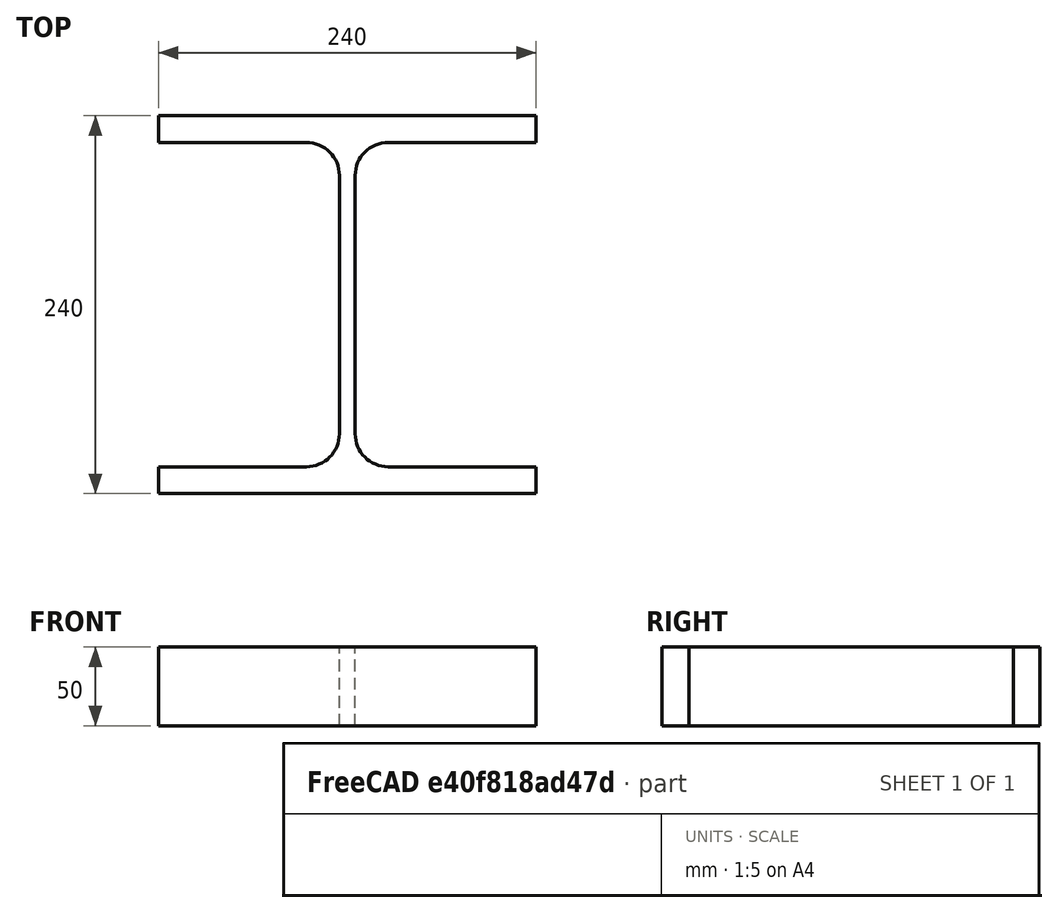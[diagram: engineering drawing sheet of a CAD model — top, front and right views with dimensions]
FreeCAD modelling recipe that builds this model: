
FCSTD DOCUMENT  (FreeCAD 0.15R4671 (Git))
Label: HE-B-Profile 240 DIN1025-2 S235JR
License: All rights reserved
LicenseURL: http://en.wikipedia.org/wiki/All_rights_reserved
objects: Sketcher::SketchObject×1, Part::Extrusion×1
note: 2 computed .brp shape members not serialized (recipe doc carries the construction recipe); baked Part::Feature solids carry a one-line shape summary decoded from their .brp

FEATURE [Sketcher::SketchObject] Sketch
  sketch-geometry (16):
    g0: LineSegment StartX=5 StartY=-82 StartZ=0 EndX=5 EndY=82 EndZ=0
    g1: LineSegment StartX=26 StartY=103 StartZ=0 EndX=120 EndY=103 EndZ=0
    g2: LineSegment StartX=120 StartY=103 StartZ=0 EndX=120 EndY=120 EndZ=0
    g3: LineSegment StartX=120 StartY=120 StartZ=0 EndX=-120 EndY=120 EndZ=0
    g4: LineSegment StartX=-120 StartY=120 StartZ=0 EndX=-120 EndY=103 EndZ=0
    g5: LineSegment StartX=-120 StartY=103 StartZ=0 EndX=-26 EndY=103 EndZ=0
    g6: LineSegment StartX=-5 StartY=82 StartZ=0 EndX=-5 EndY=-82 EndZ=0
    g7: LineSegment StartX=-26 StartY=-103 StartZ=0 EndX=-120 EndY=-103 EndZ=0
    g8: LineSegment StartX=-120 StartY=-103 StartZ=0 EndX=-120 EndY=-120 EndZ=0
    g9: LineSegment StartX=-120 StartY=-120 StartZ=0 EndX=120 EndY=-120 EndZ=0
    g10: LineSegment StartX=120 StartY=-120 StartZ=0 EndX=120 EndY=-103 EndZ=0
    g11: LineSegment StartX=120 StartY=-103 StartZ=0 EndX=26 EndY=-103 EndZ=0
    g12: ArcOfCircle CenterX=26 CenterY=82 CenterZ=0 NormalX=0 NormalY=0 NormalZ=1 Radius=21 StartAngle=1.5708 EndAngle=3.14159
    g13: ArcOfCircle CenterX=26 CenterY=-82 CenterZ=0 NormalX=0 NormalY=0 NormalZ=1 Radius=21 StartAngle=3.14159 EndAngle=4.71239
    g14: ArcOfCircle CenterX=-26 CenterY=82 CenterZ=0 NormalX=0 NormalY=0 NormalZ=1 Radius=21 StartAngle=0 EndAngle=1.5708
    g15: ArcOfCircle CenterX=-26 CenterY=-82 CenterZ=0 NormalX=0 NormalY=0 NormalZ=1 Radius=21 StartAngle=4.71239 EndAngle=6.28319
  constraints (42):
    c: Vertical(g0)
    c: Coincident(g2,g1)
    c: Vertical(g2)
    c: Coincident(g3,g2)
    c: Coincident(g4,g3)
    c: Vertical(g4)
    c: Coincident(g5,g4)
    c: Horizontal(g5)
    c: Vertical(g6)
    c: Horizontal(g7)
    c: Coincident(g8,g7)
    c: Vertical(g8)
    c: Coincident(g9,g8)
    c: Horizontal(g9)
    c: Coincident(g10,g9)
    c: Vertical(g10)
    c: Coincident(g11,g10)
    c: Horizontal(g11)
    c: Tangent(g1,g12) = 1.5708
    c: Tangent(g0,g12) = 1.5708
    c: Tangent(g0,g13) = 1.5708
    c: Tangent(g11,g13) = 1.5708
    c: Tangent(g5,g14) = 1.5708
    c: Tangent(g6,g14) = 1.5708
    c: Tangent(g6,g15) = 1.5708
    c: Tangent(g7,g15) = 1.5708
    c: Equal(g3,g9)
    c: Equal(g2,g4)
    c: Equal(g4,g8)
    c: Equal(g8,g10)
    c: Equal(g12,g14)
    c: Equal(g14,g15)
    c: Equal(g15,g13)
    c: Symmetric(g2,g3,g-2)
    c: Symmetric(g9,g8,g-2)
    c: Symmetric(g0,g6,g-2)
    c: Symmetric(g2,g9,g-1)
    c: DistanceY(g2,g9) = -240
    c: DistanceX(g3) = -240
    c: DistanceX(g0,g6) = -10
    c: DistanceY(g2) = 17
    c: Radius(g12) = 21
FEATURE [Part::Extrusion] Extrude  label="HE-B-Profile 240 DIN1025-2 S235JR"
  Base = -> Sketch
  Dir = (0,0,50)
  Solid = true
